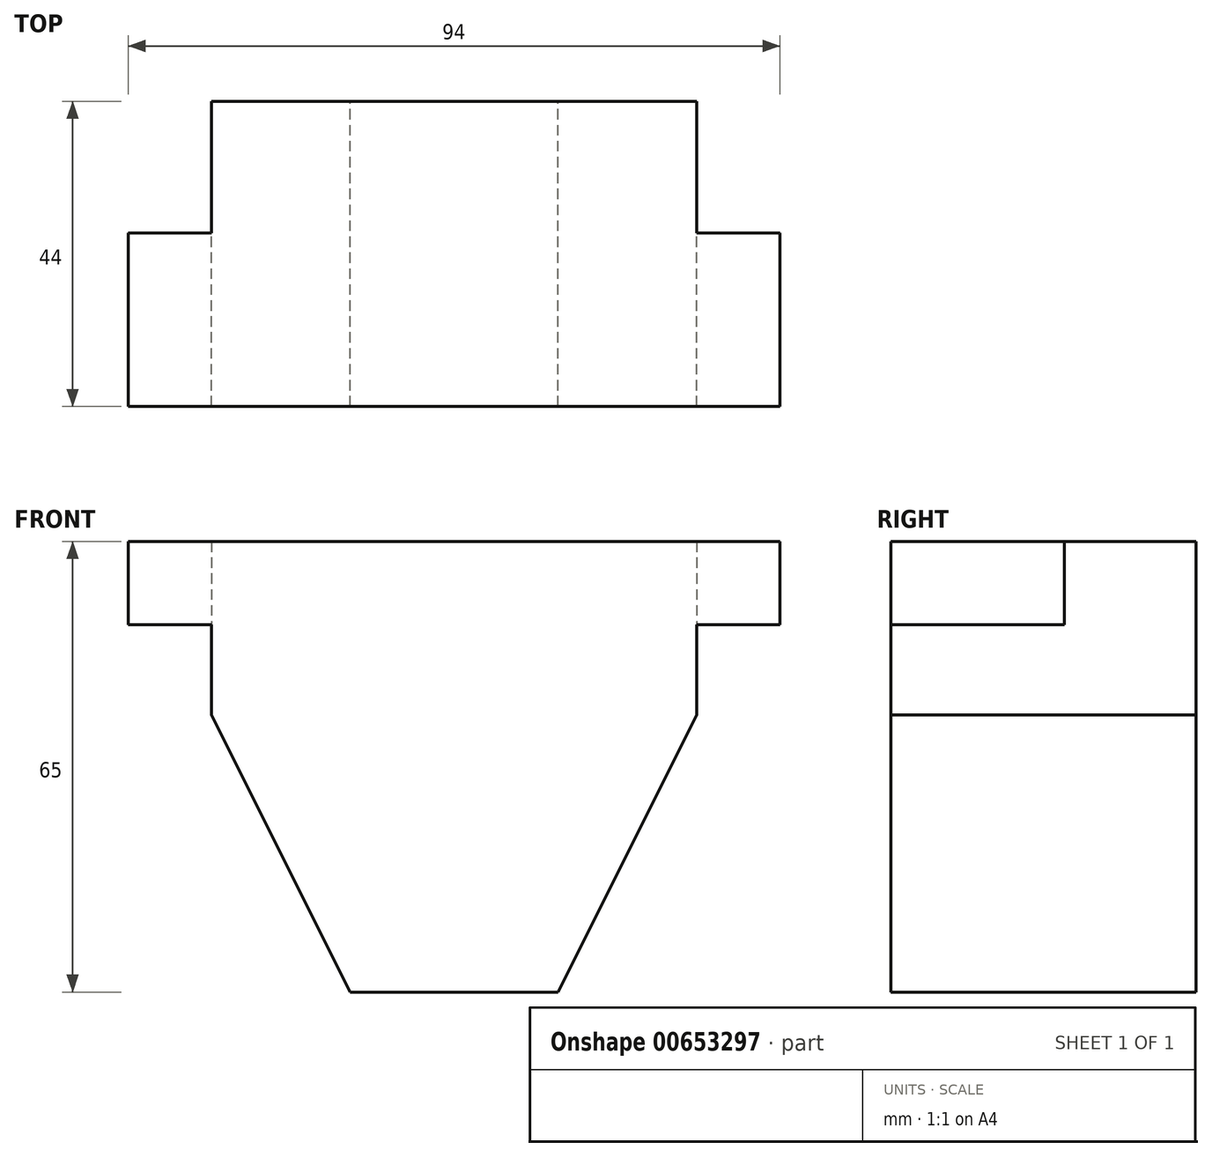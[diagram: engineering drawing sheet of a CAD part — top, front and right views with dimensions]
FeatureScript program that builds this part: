
annotation { "Feature Type Name" : "Feature", "Feature Type Description" : "" }
export const myFeature = defineFeature(function(context is Context, id is Id, definition is map)
    precondition{}
    {
        {
            var Q0;
            Q0=qCreatedBy(makeId("Front.planeOp"),FACE);
            var sketch = newSketch(context, id + "F0", { "sketchPlane" : qUnion([Q0])});
            skLineSegment(sketch, "E0.bottom", {"start": v(-15, -32.5) * mm, "end": v(15, -32.5) * mm});
            skLineSegment(sketch, "E0.top", {"start": v(-35, 32.5) * mm, "end": v(35, 32.5) * mm});
            skLineSegment(sketch, "E0.left", {"start": v(-35, 7.5) * mm, "end": v(-35, 32.5) * mm});
            skLineSegment(sketch, "E0.right", {"start": v(35, 7.5) * mm, "end": v(35, 32.5) * mm});
            skPoint(sketch, "E0.middle", {"position": v(0, 0) * mm});
            skPoint(sketch, "E1", {"position": v(-35, 7.5) * mm});
            skPoint(sketch, "E2", {"position": v(35, 7.5) * mm});
            skLineSegment(sketch, "E3", {"start": v(-35, 7.5) * mm, "end": v(-15, -32.5) * mm});
            skLineSegment(sketch, "E4", {"start": v(35, 7.5) * mm, "end": v(15, -32.5) * mm});
            skPoint(sketch, "E5.orphan", {"position": v(-35, -32.5) * mm});
            skPoint(sketch, "E6.orphan", {"position": v(35, -32.5) * mm});
            skSolve(sketch);
        }
        {
            var Q0;
            Q0=makeQuery(id+"F0.imprint","IMPRINT",FACE,{"disambiguationData":[TD([[makeQuery(id+"F0.imprint","IMPRINT",EDGE,{"derivedFrom":sQuery(id+"F0.wireOp",EDGE,"E0.bottom")}),1.0]])]});
            extrude(context, id + "F1", {"entities" : qUnion([Q0]), "depth" : 44 * mm, "offsetDistance" : 25 * mm});
        }
        {
            var Q0;
            Q0=makeQuery(id+"F1.opExtrude","SWEPT_FACE",FACE,{"disambiguationData":[OSD([sQuery(id+"F0.wireOp",EDGE,"E0.left")])]});
            var sketch = newSketch(context, id + "F2", { "sketchPlane" : qUnion([Q0])});
            skLineSegment(sketch, "E7.bottom", {"start": v(44, 32.5) * mm, "end": v(19, 32.5) * mm});
            skLineSegment(sketch, "E7.top", {"start": v(44, 20.5) * mm, "end": v(19, 20.5) * mm});
            skLineSegment(sketch, "E7.left", {"start": v(44, 32.5) * mm, "end": v(44, 20.5) * mm});
            skLineSegment(sketch, "E7.right", {"start": v(19, 32.5) * mm, "end": v(19, 20.5) * mm});
            skSolve(sketch);
        }
        {
            var Q0;
            Q0=makeQuery(id+"F2.imprint","IMPRINT",FACE,{"disambiguationData":[TD([[makeQuery(id+"F2.imprint","IMPRINT",EDGE,{"derivedFrom":sQuery(id+"F2.wireOp",EDGE,"E7.bottom")}),1.0]])]});
            extrude(context, id + "F3", {"entities" : qUnion([Q0]), "operationType" : NewBodyOperationType.ADD, "depth" : 12 * mm, "offsetDistance" : 25 * mm});
        }
        {
            var Q0;
            Q0=makeQuery(id+"F1.opExtrude","SWEPT_FACE",FACE,{"disambiguationData":[OSD([sQuery(id+"F0.wireOp",EDGE,"E0.right")])]});
            var sketch = newSketch(context, id + "F4", { "sketchPlane" : qUnion([Q0])});
            skLineSegment(sketch, "E8.bottom", {"start": v(-44, 32.5) * mm, "end": v(-19, 32.5) * mm});
            skLineSegment(sketch, "E8.top", {"start": v(-44, 20.5) * mm, "end": v(-19, 20.5) * mm});
            skLineSegment(sketch, "E8.left", {"start": v(-44, 32.5) * mm, "end": v(-44, 20.5) * mm});
            skLineSegment(sketch, "E8.right", {"start": v(-19, 32.5) * mm, "end": v(-19, 20.5) * mm});
            skSolve(sketch);
        }
        {
            var Q0;
            Q0=makeQuery(id+"F4.imprint","IMPRINT",FACE,{"disambiguationData":[TD([[makeQuery(id+"F4.imprint","IMPRINT",EDGE,{"derivedFrom":sQuery(id+"F4.wireOp",EDGE,"E8.bottom")}),-1.0]])]});
            extrude(context, id + "F5", {"entities" : qUnion([Q0]), "operationType" : NewBodyOperationType.ADD, "depth" : 12 * mm, "offsetDistance" : 25 * mm});
        }
    });
